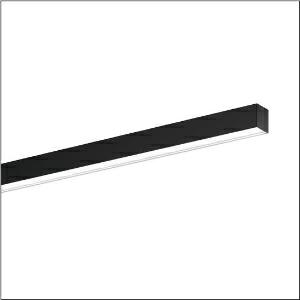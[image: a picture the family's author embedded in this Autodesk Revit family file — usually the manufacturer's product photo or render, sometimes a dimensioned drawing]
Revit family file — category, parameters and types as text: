
# Revit family: silica_21_51mx23da34bb
name_source: partatom
category: Lighting Fixtures
units: mm (PartAtom-declared; Revit-internal decimal feet)

## family parameters
Cut with Voids When Loaded = No
Host = Face
Light Source = No
Part Type = Normal
Room Calculation Point = No
Round Connector Dimension = Use Diameter
Shared = No

## types (1)
- --- (1 x LED, 3280 lm, 24.1 W, 3000K)
    Apparent Load = 24 VA
    CIE Flux Codes = 78 96 99 100 100
    Color Rendering = 80
    Color Temperature = 3000K
    Default Elevation = 1800 mm
    Description = Silica 21, office luminaire, primary optical cover: prismatic diffuser, of PMMA, CAT 2 (L<= 3000cd/m²), light emission: direct distribution, primary light characteristic: symmetric, installation type: surface-mounted, LED, rated luminous flux: 3.280lm, luminous efficacy: 136lm/W, light colour: 830, colour temperature: 3000K, control gear: DALI 2, with terminal, 3+2-pole, max. 2.5mm², mains connection: 220..240V, AC, 50/60Hz, rated input power: 24.1W, luminaire housing, of aluminium, matt jet black (RAL 9005), length: 1.204mm, width: 53mm, height: 53mm, protection rating (complete): IP20, insulation class (complete): insulation class I (protective earthing), certification: CE, permissible operating ambient temperature: 0..+35°C, standard: EN 50419, packaging unit: 1 piece
    Height = 53 mm
    Lamp = 1 x LED
    Lamp Light Flux = 3280 lm
    Lamp Power = 24.1 W
    Lamp count = 1
    Length = 1204 mm
    Luminous efficacy = 136 lm/W
    Manufacturer = Siteco
    ModVariant = No
    Model = 51MX23DA34BB
    Mounting Place = Ceiling
    Mounting Type = Surface mounted
    Number of Poles = 1
    OnlyDefault = Yes
    Power Factor = 1
    Product Name = Silica 21
    Product group = office luminaire | ceiling mounted
    ProductGroupID = 301
    Protection Class = Protection class I
    Protection Degree = IP 20
    RLX_Detail_Level = 1
    RLX_Emergency_Light_Flux = 0 lm
    RLX_Emergency_Type = 0
    RLX_Emergency_Type_DB = No
    RlxData = <blob elided: 23773 chars, md5=ea915c3a>
    Socket = socket
    Standby Power = 0 W
    System Light Flux = 3280 lm
    System Power = 24 W
    Type Comments = factory setting: luminous flux: 100 % | dim-lin: 254 | 345 mA
    Type Image = l_1335925.jpg
    URL = http://relux.com
    VarID = @adj_029723
    Voltage = 0 V
    Weight = 0.00 kg
    Width = 53 mm

## geometry (parser evidence)
native form markers: Blend x4, Sweep x9
no freeform markers — native parametric forms only
